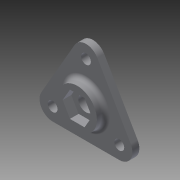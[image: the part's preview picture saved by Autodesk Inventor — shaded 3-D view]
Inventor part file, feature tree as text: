
AUTODESK INVENTOR PART (.ipt)
format: ipt  version: 2013 (Build 170138000, 138)  size: 149,504 bytes
history: native  units: in
note: dims shown in document units (in); Inventor stores cm internally (conversion verified against a paired STEP export)
features: extrude x3, sketch x3, fillet x2
ambient origin geometry x8: Origin, YZ Plane, XZ Plane, XY Plane, X Axis, Y Axis, Z Axis, Center Point
bodies: Solid1 (feature_tree)
feature tree (8):
  extrude  "Extrusion1"  Depth=0.1772in
  extrude  "Extrusion2"  Depth=0.2756in
  fillet  "Fillet1"  Radius=0.4724in
  extrude  "Extrusion3"  Depth=0.2362in
  fillet  "Fillet2"  Radius=0.125in
  sketch  "Sketch1"  dims[d7=1.2008in d8=0.1772in]
  sketch  "Sketch2"  dims[d9=1.1811in d11=360.0deg d13=0.2756in d14=0.4724in]
  sketch  "Sketch3"  dims[d15=1.1811in d17=360.0deg d19=0.2362in d20=0.125in d21=0.0in d22=0.5118in d23=0.1772in d24=0.0in d25=0.1181in d26=0.4567in d27=0.7087in d28=0.1575in d29=0.0in d30=0.0787in]
